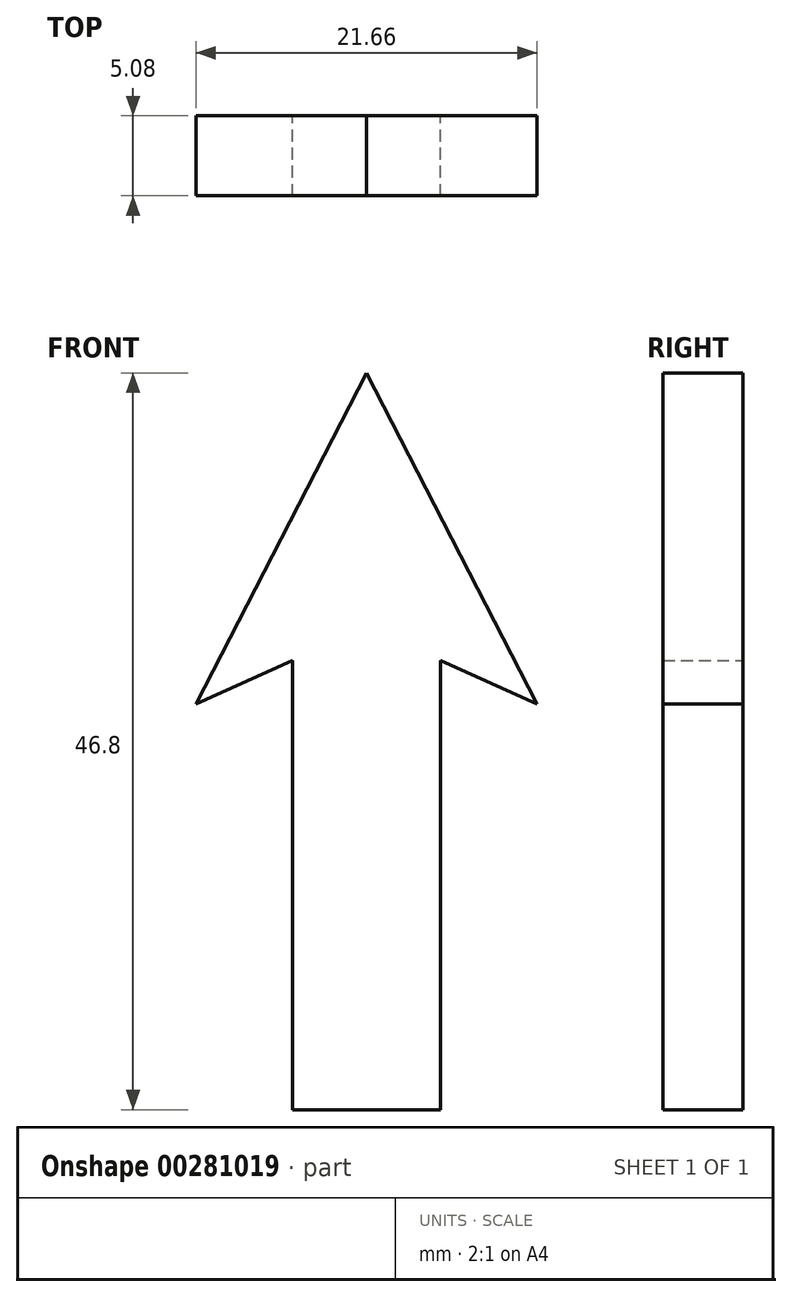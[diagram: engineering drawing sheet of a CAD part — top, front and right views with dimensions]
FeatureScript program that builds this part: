
annotation { "Feature Type Name" : "Feature", "Feature Type Description" : "" }
export const myFeature = defineFeature(function(context is Context, id is Id, definition is map)
    precondition{}
    {
        {
            var Q0;
            Q0=qCreatedBy(makeId("Front.planeOp"),FACE);
            var sketch = newSketch(context, id + "F0", { "sketchPlane" : qUnion([Q0])});
            skLineSegment(sketch, "E0", {"start": v(0, 0) * mm, "end": v(4.7, 0) * mm});
            skLineSegment(sketch, "E1", {"start": v(4.7, 0) * mm, "end": v(4.7, 28.53) * mm});
            skLineSegment(sketch, "E2", {"start": v(4.7, 28.53) * mm, "end": v(10.83, 25.78) * mm});
            skLineSegment(sketch, "E3", {"start": v(10.83, 25.78) * mm, "end": v(0, 46.8) * mm});
            skLineSegment(sketch, "E4", {"start": v(0, 46.8) * mm, "end": v(0, 0) * mm});
            skSolve(sketch);
        }
        {
            var Q0;
            Q0=makeQuery(id+"F0.imprint","IMPRINT",FACE,{"disambiguationData":[TD([[makeQuery(id+"F0.imprint","IMPRINT",EDGE,{"derivedFrom":sQuery(id+"F0.wireOp",EDGE,"E0")}),1.0]])]});
            extrude(context, id + "F1", {"entities" : qUnion([Q0]), "depth" : 5.08 * mm, "symmetric" : true});
        }
        {
            var Q0;
            Q0=makeQuery(id+"F1.opExtrude","SWEPT_BODY",BODY,{"disambiguationData":[OSD([sQuery(id+"F0.wireOp",EDGE,"E0"),sQuery(id+"F0.wireOp",EDGE,"E1"),sQuery(id+"F0.wireOp",EDGE,"E2"),sQuery(id+"F0.wireOp",EDGE,"E3"),sQuery(id+"F0.wireOp",EDGE,"E4")])]});
            var Q1;
            Q1=makeQuery(id+"F1.opExtrude","SWEPT_FACE",FACE,{"disambiguationData":[OSD([sQuery(id+"F0.wireOp",EDGE,"E4")])]});
            mirror(context, id + "F2", {"operationType" : NewBodyOperationType.ADD, "entities" : qUnion([Q0]), "mirrorPlane" : qUnion([Q1])});
        }
    });
